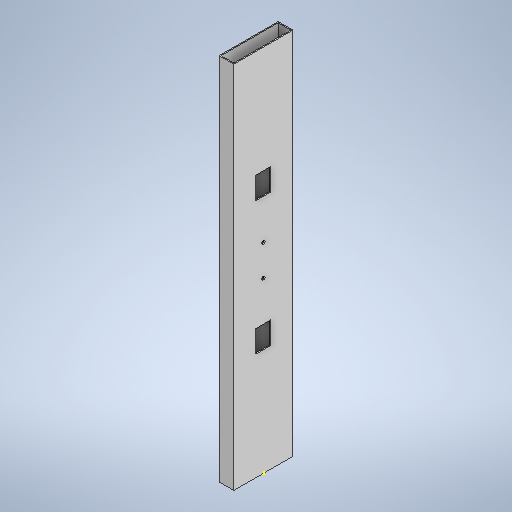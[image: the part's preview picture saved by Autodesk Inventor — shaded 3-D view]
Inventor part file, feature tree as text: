
AUTODESK INVENTOR PART (.ipt)
format: ipt  version: 2025 (Build 290162000, 162)  size: 304,640 bytes
history: native  units: mm
features: sketch x7, extrude x4
ambient origin geometry x8: Origin, YZ Plane, XZ Plane, XY Plane, X Axis, Y Axis, Z Axis, Center Point
bodies: Body1 (feature_tree)
feature tree (11):
  extrude  "Wyciągnięcie proste2"  Depth=20.0mm
  extrude  "Wyciągnięcie proste3"  Depth=80.0mm
  sketch  "Szkic4"
  sketch  "Szkic5"
  sketch  "Szkic6"
  extrude  "Wyciągnięcie proste4"  Depth=1.4mm
  extrude  "Wyciągnięcie proste5"  Depth=1.4mm
  sketch  "Szkic2"
  sketch  "Szkic3"
  sketch  "Szkic7"
  sketch  "Szkic8"
